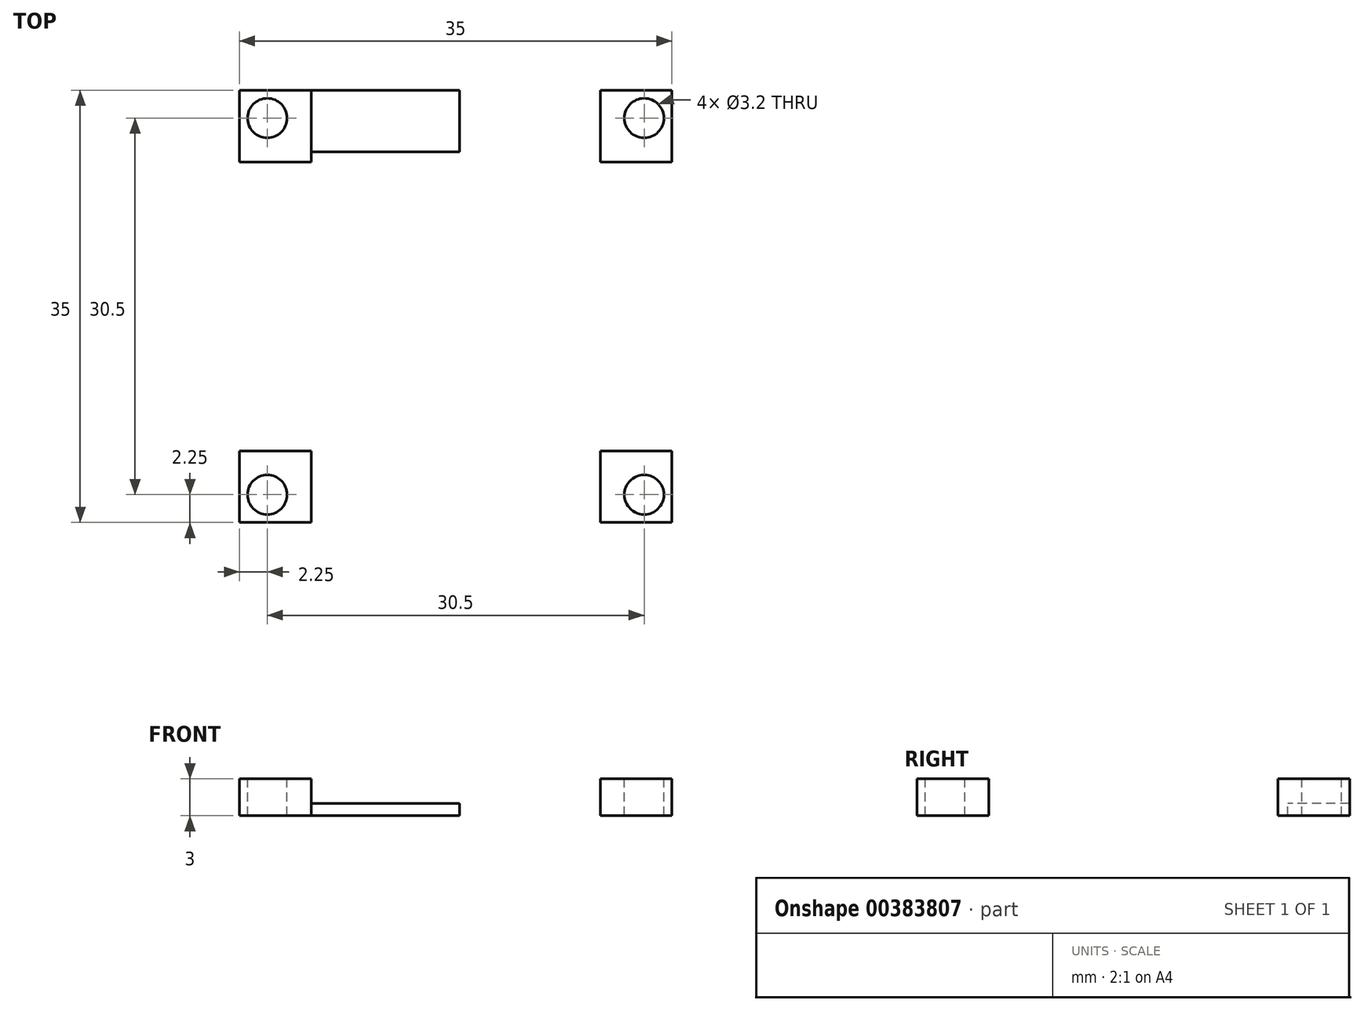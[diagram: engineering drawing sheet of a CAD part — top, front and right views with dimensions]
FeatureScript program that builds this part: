
annotation { "Feature Type Name" : "Feature", "Feature Type Description" : "" }
export const myFeature = defineFeature(function(context is Context, id is Id, definition is map)
    precondition{}
    {
        {
            var Q0;
            Q0=qCreatedBy(makeId("Top.planeOp"),FACE);
            var sketch = newSketch(context, id + "F0", { "sketchPlane" : qUnion([Q0])});
            skLineSegment(sketch, "E0.bottom", {"start": v(17.5, 17.5) * mm, "end": v(-17.5, 17.5) * mm});
            skLineSegment(sketch, "E0.top", {"start": v(17.5, -17.5) * mm, "end": v(-17.5, -17.5) * mm});
            skLineSegment(sketch, "E0.left", {"start": v(17.5, 17.5) * mm, "end": v(17.5, -17.5) * mm});
            skLineSegment(sketch, "E0.right", {"start": v(-17.5, 17.5) * mm, "end": v(-17.5, -17.5) * mm});
            skPoint(sketch, "E0.middle", {"position": v(0, 0) * mm});
            skLineSegment(sketch, "E1.bottom", {"start": v(15.25, 15.25) * mm, "end": v(-15.25, 15.25) * mm, "construction": true});
            skLineSegment(sketch, "E1.top", {"start": v(15.25, -15.25) * mm, "end": v(-15.25, -15.25) * mm, "construction": true});
            skLineSegment(sketch, "E1.left", {"start": v(15.25, 15.25) * mm, "end": v(15.25, -15.25) * mm, "construction": true});
            skLineSegment(sketch, "E1.right", {"start": v(-15.25, 15.25) * mm, "end": v(-15.25, -15.25) * mm, "construction": true});
            skCircle(sketch, "E2", {"center": v(-15.25, 15.25) * mm, "radius": 1.6 * mm});
            skCircle(sketch, "E3", {"center": v(-15.25, -15.25) * mm, "radius": 1.6 * mm});
            skCircle(sketch, "E4", {"center": v(15.25, -15.25) * mm, "radius": 1.6 * mm});
            skCircle(sketch, "E5", {"center": v(15.25, 15.25) * mm, "radius": 1.6 * mm});
            skLineSegment(sketch, "E6.bottom", {"start": v(-17.5, -17.5) * mm, "end": v(-11.7, -17.5) * mm});
            skLineSegment(sketch, "E6.top", {"start": v(-17.5, -11.7) * mm, "end": v(-11.7, -11.7) * mm});
            skLineSegment(sketch, "E6.left", {"start": v(-17.5, -17.5) * mm, "end": v(-17.5, -11.7) * mm});
            skLineSegment(sketch, "E6.right", {"start": v(-11.7, -17.5) * mm, "end": v(-11.7, -11.7) * mm});
            skLineSegment(sketch, "E7.bottom", {"start": v(17.5, -17.5) * mm, "end": v(11.7, -17.5) * mm});
            skLineSegment(sketch, "E7.top", {"start": v(17.5, -11.7) * mm, "end": v(11.7, -11.7) * mm});
            skLineSegment(sketch, "E7.left", {"start": v(17.5, -17.5) * mm, "end": v(17.5, -11.7) * mm});
            skLineSegment(sketch, "E7.right", {"start": v(11.7, -17.5) * mm, "end": v(11.7, -11.7) * mm});
            skLineSegment(sketch, "E8.bottom", {"start": v(17.5, 17.5) * mm, "end": v(11.7, 17.5) * mm});
            skLineSegment(sketch, "E8.top", {"start": v(17.5, 11.7) * mm, "end": v(11.7, 11.7) * mm});
            skLineSegment(sketch, "E8.left", {"start": v(17.5, 17.5) * mm, "end": v(17.5, 11.7) * mm});
            skLineSegment(sketch, "E8.right", {"start": v(11.7, 17.5) * mm, "end": v(11.7, 11.7) * mm});
            skLineSegment(sketch, "E9.bottom", {"start": v(-17.5, 17.5) * mm, "end": v(-11.7, 17.5) * mm});
            skLineSegment(sketch, "E9.top", {"start": v(-17.5, 11.7) * mm, "end": v(-11.7, 11.7) * mm});
            skLineSegment(sketch, "E9.left", {"start": v(-17.5, 17.5) * mm, "end": v(-17.5, 11.7) * mm});
            skLineSegment(sketch, "E9.right", {"start": v(-11.7, 17.5) * mm, "end": v(-11.7, 11.7) * mm});
            skLineSegment(sketch, "E10.bottom", {"start": v(11.7, -17.5) * mm, "end": v(2.7, -17.5) * mm});
            skLineSegment(sketch, "E10.top", {"start": v(11.7, -12.5) * mm, "end": v(2.7, -12.5) * mm});
            skLineSegment(sketch, "E10.left", {"start": v(11.7, -17.5) * mm, "end": v(11.7, -12.5) * mm});
            skLineSegment(sketch, "E10.right", {"start": v(2.7, -17.5) * mm, "end": v(2.7, -12.5) * mm});
            skLineSegment(sketch, "E11.bottom", {"start": v(-17.5, 11.7) * mm, "end": v(-12.5, 11.7) * mm});
            skLineSegment(sketch, "E11.top", {"start": v(-17.5, -11.7) * mm, "end": v(-12.5, -11.7) * mm});
            skLineSegment(sketch, "E11.left", {"start": v(-17.5, 11.7) * mm, "end": v(-17.5, -11.7) * mm});
            skLineSegment(sketch, "E11.right", {"start": v(-12.5, 11.7) * mm, "end": v(-12.5, -11.7) * mm});
            skLineSegment(sketch, "E12.bottom", {"start": v(-11.7, 17.5) * mm, "end": v(0.3, 17.5) * mm});
            skLineSegment(sketch, "E12.top", {"start": v(-11.7, 12.5) * mm, "end": v(0.3, 12.5) * mm});
            skLineSegment(sketch, "E12.left", {"start": v(-11.7, 17.5) * mm, "end": v(-11.7, 12.5) * mm});
            skLineSegment(sketch, "E12.right", {"start": v(0.3, 17.5) * mm, "end": v(0.3, 12.5) * mm});
            skSolve(sketch);
        }
        {
            var Q0;
            Q0=makeQuery(id+"F0.imprint","IMPRINT",FACE,{"disambiguationData":[TD([[makeQuery(id+"F0.imprint","IMPRINT",EDGE,{"derivedFrom":sQuery(id+"F0.wireOp",EDGE,"E0.bottom")}),1.0]])]});
            var Q1;
            Q1=makeQuery(id+"F0.imprint","IMPRINT",FACE,{"disambiguationData":[TD([[makeQuery(id+"F0.imprint","IMPRINT",EDGE,{"derivedFrom":sQuery(id+"F0.wireOp",EDGE,"E3")}),-1.0]])]});
            var Q2;
            Q2=makeQuery(id+"F0.imprint","IMPRINT",FACE,{"disambiguationData":[TD([[makeQuery(id+"F0.imprint","IMPRINT",EDGE,{"derivedFrom":sQuery(id+"F0.wireOp",EDGE,"E4")}),-1.0]])]});
            var Q3;
            Q3=makeQuery(id+"F0.imprint","IMPRINT",FACE,{"disambiguationData":[TD([[makeQuery(id+"F0.imprint","IMPRINT",EDGE,{"derivedFrom":sQuery(id+"F0.wireOp",EDGE,"E5")}),-1.0]])]});
            var Q4;
            Q4=makeQuery(id+"F0.imprint","IMPRINT",FACE,{"disambiguationData":[TD([[makeQuery(id+"F0.imprint","IMPRINT",EDGE,{"derivedFrom":sQuery(id+"F0.wireOp",EDGE,"E2")}),-1.0]])]});
            extrude(context, id + "F1", {"entities" : qUnion([Q0, Q1, Q2, Q3, Q4]), "oppositeDirection" : true, "depth" : 1 * mm, "offsetDistance" : 25 * mm});
        }
        {
            var Q0;
            Q0=makeQuery(id+"F0.imprint","IMPRINT",FACE,{"disambiguationData":[TD([[makeQuery(id+"F0.imprint","IMPRINT",EDGE,{"derivedFrom":sQuery(id+"F0.wireOp",EDGE,"E3")}),-1.0]])]});
            var Q1;
            Q1=makeQuery(id+"F0.imprint","IMPRINT",FACE,{"disambiguationData":[TD([[makeQuery(id+"F0.imprint","IMPRINT",EDGE,{"derivedFrom":sQuery(id+"F0.wireOp",EDGE,"E2")}),-1.0]])]});
            var Q2;
            Q2=makeQuery(id+"F0.imprint","IMPRINT",FACE,{"disambiguationData":[TD([[makeQuery(id+"F0.imprint","IMPRINT",EDGE,{"derivedFrom":sQuery(id+"F0.wireOp",EDGE,"E5")}),-1.0]])]});
            var Q3;
            Q3=makeQuery(id+"F0.imprint","IMPRINT",FACE,{"disambiguationData":[TD([[makeQuery(id+"F0.imprint","IMPRINT",EDGE,{"derivedFrom":sQuery(id+"F0.wireOp",EDGE,"E4")}),-1.0]])]});
            extrude(context, id + "F2", {"entities" : qUnion([Q0, Q1, Q2, Q3]), "operationType" : NewBodyOperationType.ADD, "depth" : 2 * mm, "offsetDistance" : 25 * mm});
        }
    });
